# Revit family: Lighting_Pendants_Focus-Lighting_Pelee-Pendant-with-uplight
name_source: partatom
category: Lighting Fixtures
revit_build: Autodesk Revit 2015 (Build: 20140903_1530(x64)
units: mm (PartAtom-declared; Revit-internal decimal feet)

## types (1)
- 1840-1927
    BIMobject category = Pendants
    BIMobject category code = lighting-pendants
    BIMobject main category = Lighting
    BIMobject main category code = lighting
    Brand url = http://focus-lighting.dk
    Classification = IP20 class I
    Coating = White or grey metallic
    Color Filter = 16777215
    Colour = Grey metallic FB20D058
    Colour accuracy = 3 steps SDCM
    Colour rendering = min 90 Ra
    Design country = Denmark
    Dimming = no dimming
    Dimming Lamp Color Temperature Shift = <None>
    Driver = Helvar LED driver 350-700 mA
    Driver Operational life = min 50.000 hours
    Edition number = 1
    Emit Shape Visible in Rendering = No
    Emit from Circle Diameter = 330 mm
    IFC Classification = Lamp
    LED = 324 mm board
    LED Operational life = min 50.000 hours at ta max 25° C L80B10
    Lead = 3 m white PKLJ
    Manufacturer country = Denmark
    Manufacturer name = Focus Lighting
    Masterformat 2014 Code = 12 43 13
    Masterformat 2014 Description = Lamps
    Material = Cast aluminium
    Material main = Aluminium
    Material secondary = Polycarbonate
    Min Distance from ceiling = 283 mm  [stored 0.928478 ft]
    NBS Reference Code = 49
    NBS Reference Description = Luminaires And Lamps
    OmniClass Code = 23-35 45 15
    OmniClass Description = Lamps
    Output ratio = 76%
    Photometric Web File = Pelée Pendel Ø385 with uplight_18W_927.IES
    Product Guid = 8fa08f4e-9f70-4035-a035-1ec25de53564
    Product SKU = Pelee-pendel
    Product data url = https://bimobject.com
    Product family = Outdoor
    Product group = Pendant
    Product url = http://www.focus-lighting.dk
    QR code = http://bimobject.com
    Shade = Opal-white acrylate PMMA
    Tilt Angle = 90.00°
    Total consumption = 17-18 W (500 mA)
    UNSPSC Code = 391016
    Uniclass 1.4 Code = L7474
    Uniclass 1.4 Description = Lamps
    Uniclass 2.0 Code = PR-49
    Uniclass 2.0 Description = Luminaires And Lamps
    Uniclass 2015 Code = Pr_70_70_46
    Uniclass 2015 Name = Lamps
    Weight = 4 kg

note: [stored X ft] marks values corroborated as IEEE doubles in the binary element streams (Revit-internal decimal feet)

## geometry (parser evidence)
native form markers: Sweep x6
no freeform markers — native parametric forms only
